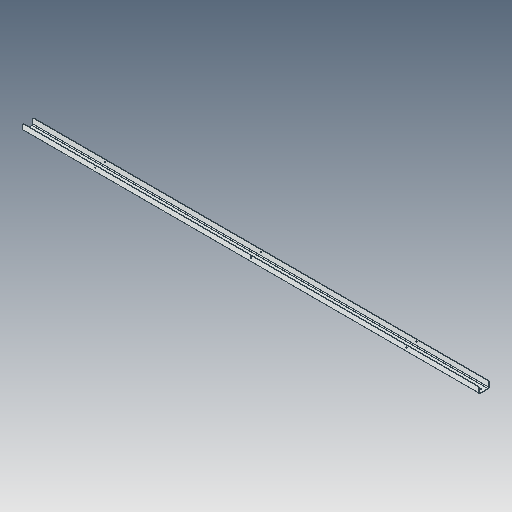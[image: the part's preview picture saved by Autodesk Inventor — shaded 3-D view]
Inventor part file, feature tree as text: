
AUTODESK INVENTOR PART (.ipt)
format: ipt  version: 2023.5 (Build 275446000, 446)  size: 109,568 bytes
history: native  units: in
note: dims shown in document units (in); Inventor stores cm internally (conversion verified against a paired STEP export)
features: fillet x1
ambient origin geometry x8: Origin, YZ Plane, XZ Plane, XY Plane, X Axis, Y Axis, Z Axis, Center Point
bodies: Solid1 (feature_tree)
feature tree (1):
  fillet  "Fillet1"  [1 undecoded]
note: 1 required parameter value undecoded (feature->parameter linkage not recoverable at this tier; creation-order binding heuristic only, values carry confidence <= 0.55)
